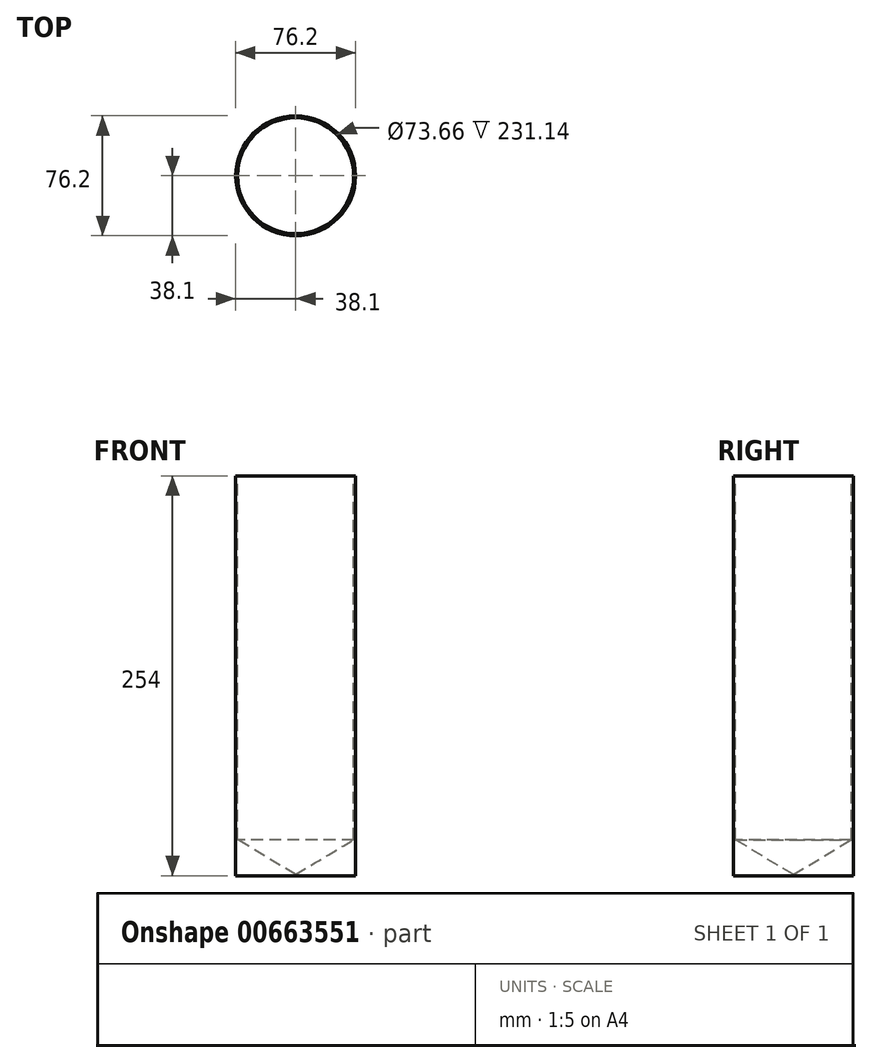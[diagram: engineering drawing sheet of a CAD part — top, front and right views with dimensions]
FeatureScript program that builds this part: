
annotation { "Feature Type Name" : "Feature", "Feature Type Description" : "" }
export const myFeature = defineFeature(function(context is Context, id is Id, definition is map)
    precondition{}
    {
        {
            var Q0;
            Q0=qCreatedBy(makeId("Top.planeOp"),FACE);
            var sketch = newSketch(context, id + "F0", { "sketchPlane" : qUnion([Q0])});
            skCircle(sketch, "E0", {"center": v(0, 0) * mm, "radius": 38.1 * mm});
            skSolve(sketch);
        }
        {
            var Q0;
            Q0 = qSketchRegion(id + "F0", true);
            extrude(context, id + "F1", {"entities" : qUnion([Q0]), "oppositeDirection" : true, "depth" : 254 * mm, "offsetDistance" : 25.4 * mm});
        }
        {
            var Q0;
            Q0=sQuery(id+"F0.wireOp",VERTEX,"E0.center");
            var Q1;
            Q1=makeQuery(id+"F1.opExtrude","SWEPT_BODY",BODY,{"disambiguationData":[OSD([sQuery(id+"F0.wireOp",EDGE,"E0")])]});
            hole(context, id + "F2", {"style" : HoleStyle.SIMPLE, "endStyle" : HoleEndStyle.BLIND, "holeDiameter" : 73.66 * mm, "majorDiameter" : 6.35 * mm, "holeDepth" : 231.14 * mm, "isTappedThrough" : true, "tappedDepth" : 12.7 * mm, "tapClearance" : 3, "startFromSketch" : true, "locations" : qUnion([Q0]), "scope" : qUnion([Q1])});
        }
    });
